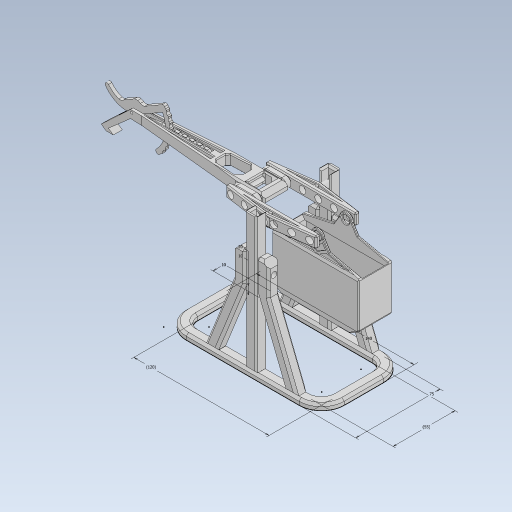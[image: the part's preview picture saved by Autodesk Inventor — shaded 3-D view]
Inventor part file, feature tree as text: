
AUTODESK INVENTOR PART (.ipt)
format: ipt  version: 2023 (Build 270158030, 158C)  size: 2,156,544 bytes
history: native  units: mm
features: extrude x40, chamfer x35, sketch x32, other x22, projected_geometry x18, fillet x12, mirror x11, plane x5, pattern_circular x2
ambient origin geometry x8: Origin, YZ Plane, XZ Plane, XY Plane, X Axis, Y Axis, Z Axis, Center Point
bodies: SOLID_WEIGHT (feature_tree)
feature tree (177):
  other  "baseplate"
  sketch  "Sketch1"  dims[d0=75.0mm d1=140.0mm]
  extrude  "Extrusion1"  Depth=140.0mm
  extrude  "Extrusion2"  Depth=10.0mm
  sketch  "Sketch3"  dims[d4=20.0mm d5=5.0mm d6=0.0mm]
  extrude  "Extrusion5"  Depth=5.0mm TaperAngle=0.0deg
  extrude  "Extrusion6"  Depth=2.0mm
  extrude  "Extrusion3"  Depth=3.0mm
  extrude  "Extrusion7"  Depth=10.0mm
  extrude  "Extrusion9"  TaperAngle=0.0deg  [1 undecoded]
  extrude  "Extrusion10"  Depth=120.0mm
  extrude  "Extrusion11"  Depth=0.01mm
  extrude  "Extrusion29"  Depth=10.0mm
  other  "center-mirror-plane"
  other  "Work Point1"
  plane  "Work Plane2"
  extrude  "Extrusion12"  Depth=25.0mm
  extrude  "Extrusion13"  Depth=5.0mm TaperAngle=0.0deg
  extrude  "Extrusion14"  Depth=10.0mm
  extrude  "Extrusion15"  Depth=10.0mm TaperAngle=0.0deg
  extrude  "Extrusion30"  Depth=5.0mm
  extrude  "Extrusion31"  Depth=6.5mm
  plane  "Work Plane5"
  extrude  "Extrusion32"  Depth=1.75mm
  extrude  "Extrusion33"  Depth=6.5mm
  extrude  "Extrusion34"  Depth=10.0mm
  fillet  "Fillet4"  Radius=3.2mm
  chamfer  "Chamfer37"  Distance=10.0mm
  extrude  "Extrusion35"  Depth=4.0mm
  chamfer  "Chamfer38"  [1 undecoded]
  fillet  "Fillet11"  Radius=21.0mm
  chamfer  "Chamfer39"  Distance=125.0mm
  fillet  "Fillet12"  Radius=10.0mm
  extrude  "Extrusion36"  Depth=1.5mm
  fillet  "Fillet5"  Radius=12.0mm
  extrude  "ratchet-extrusion"  TaperAngle=0.0deg  [1 undecoded]
  sketch  "Sketch51"  dims[d101=6.5mm]
  extrude  "Extrusion45"  Depth=1.5mm
  extrude  "Extrusion46"  Depth=1.5mm
  pattern_circular  "Circular Pattern3"  [2 undecoded]
  pattern_circular  "Circular Pattern4"  Angle=45.0deg  [1 undecoded]
  fillet  "Fillet13"  Radius=1.0mm
  fillet  "Fillet15"  Radius=1.5mm
  fillet  "Fillet10"  Radius=2.5mm
  extrude  "Extrusion17"  Depth=1.5mm
  extrude  "Extrusion26"  Depth=1.5mm
  extrude  "Extrusion38"  TaperAngle=0.0deg  [1 undecoded]
  extrude  "Extrusion47"  Depth=1.5mm
  fillet  "Fillet19"  Radius=2.0mm
  fillet  "Fillet16"  Radius=1.0mm
  chamfer  "Chamfer1"  Distance=1.5mm Angle=45.0deg
  chamfer  "Chamfer2"  Distance=1.5mm Angle=45.0deg
  chamfer  "Chamfer4"  Distance=2.0mm Angle=45.0deg
  chamfer  "Chamfer56"  Distance=1.5mm Angle=45.0deg
  extrude  "Extrusion19"  Depth=1.5mm
  chamfer  "Chamfer5"  Distance=8.0mm
  chamfer  "Chamfer8"  Distance=5.0mm
  chamfer  "Chamfer9"  Distance=28.0mm
  chamfer  "Chamfer10"  Distance=6.0mm
  extrude  "Extrusion39"  Depth=1.5mm
  mirror  "Mirror12"
  chamfer  "Chamfer11"  Distance=5.0mm
  chamfer  "Chamfer50"  Distance=28.0mm
  chamfer  "Chamfer12"  Distance=8.0mm
  plane  "Work Plane4"
  extrude  "CW-extrusion"  Depth=1.5mm
  mirror  "Mirror3"
  extrude  "Extrusion21"  Depth=1.5mm
  extrude  "Extrusion22"  Depth=1.5mm TaperAngle=0.0deg
  mirror  "Mirror4"
  chamfer  "Chamfer13"  Distance=2.0mm
  extrude  "Extrusion23"  Depth=1.5mm TaperAngle=0.0deg
  mirror  "Mirror5"
  chamfer  "Chamfer31"  Distance=1.5mm Angle=45.0deg
  chamfer  "Chamfer14"  Distance=1.5mm
  chamfer  "Chamfer17"  Distance=1.0mm Angle=45.0deg
  chamfer  "Chamfer18"  Distance=0.5mm Angle=45.0deg
  extrude  "Extrusion24"  Depth=0.5mm TaperAngle=45.0deg
  extrude  "Extrusion25"  TaperAngle=0.0deg  [1 undecoded]
  chamfer  "Chamfer20"  Distance=1.0mm
  chamfer  "Chamfer49"  Distance=1.0mm
  chamfer  "Chamfer21"  [1 undecoded]
  extrude  "Extrusion40"  Depth=4.0mm TaperAngle=45.0deg
  extrude  "Extrusion41"  Depth=1.5mm TaperAngle=45.0deg
  chamfer  "Chamfer22"  Distance=1.2mm Angle=45.0deg
  chamfer  "Chamfer44"  Distance=1.2mm
  chamfer  "Chamfer45"  Distance=3.0mm
  fillet  "Fillet3"  Radius=2.0mm
  mirror  "Mirror2"
  mirror  "Mirror1"
  plane  "Work Plane3"
  mirror  "Mirror6"
  mirror  "Mirror7"
  mirror  "Mirror8"
  chamfer  "Chamfer26"  Distance=2.0mm
  chamfer  "Chamfer27"  Distance=2.0mm
  extrude  "Extrusion43"  Depth=1.5mm
  mirror  "Mirror10"
  chamfer  "Chamfer47"  Distance=15.996982mm
  extrude  "Extrusion42"  Depth=1.5mm
  chamfer  "Chamfer48"  Distance=6.0mm
  mirror  "Mirror11"
  plane  "Work Plane6"
  chamfer  "Chamfer51"  Distance=6.0mm
  chamfer  "Chamfer52"  Distance=6.0mm
  fillet  "Fillet17"  Radius=5.0mm
  chamfer  "Chamfer53"  Distance=5.0mm
  chamfer  "Chamfer54"  Distance=14.0mm
  chamfer  "Chamfer55"  Distance=14.0mm
  fillet  "Fillet18"  [1 undecoded]
  chamfer  "Chamfer57"  Distance=3.5mm Angle=45.0deg
  sketch  "Sketch2"  dims[d2=10.0mm d3=10.0mm]
  sketch  "Sketch4"  dims[d7=6.0mm d9=2.0mm]
  projected_geometry  "Projected Loop1"
  other  "A-frame"
  sketch  "Sketch7"  dims[d10=10.0mm d11=3.0mm]
  projected_geometry  "Projected Loop2"
  other  "upright"
  sketch  "Sketch9"  dims[d12=1.75mm d13=6.0mm d14=10.0mm]
  projected_geometry  "Projected Loop3"
  sketch  "Sketch10"  dims[d15=60.0mm d16=0.0mm d17=0.0mm]
  sketch  "Sketch12"  dims[d18=55.0mm d19=120.0mm]
  sketch  "Sketch13"  dims[d22=0.1mm d23=0.01mm]
  sketch  "Sketch14"  dims[d24=5.0mm d25=0.0mm d38=10.0mm]
  other  "pivot"
  sketch  "Sketch16"  dims[d39=25.0mm d40=25.0mm]
  other  "throw-arm-top"
  sketch  "Sketch18"  dims[d41=0.1mm d42=5.0mm d43=5.0mm d44=0.0mm d45=0.0mm]
  sketch  "Sketch20"  dims[d47=10.0mm d50=10.0mm]
  sketch  "Sketch22"  dims[d51=120.0mm d52=0.0mm d53=10.0mm d54=0.0mm]
  other  "counterweight"
  projected_geometry  "Projected Loop5"
  sketch  "Sketch26"  dims[d60=5.0mm d61=5.0mm]
  projected_geometry  "Projected Loop6"
  sketch  "Sketch27"  dims[d64=0.0mm d65=0.0mm d66=6.5mm]
  projected_geometry  "Projected Loop7"
  sketch  "Sketch30"  dims[d67=1.75mm d68=1.75mm]
  other  "Pattern of pivot:1"
  other  "pivot-mirror"
  other  "Pattern of upright:2"
  other  "upright-mirror"
  other  "Pattern of A-frame:3"
  other  "A-frame-b"
  other  "Pattern of A-frame:4"
  other  "A-frame-c"
  other  "Pattern of A-frame-b:5"
  other  "A-frame-d"
  sketch  "Sketch31"  dims[d69=11.0mm d70=6.5mm]
  projected_geometry  "Projected Loop8"
  sketch  "Sketch32"  dims[d71=7.0mm d72=0.0mm d73=6.0mm d74=3.2mm d75=10.0mm d76=0.0mm]
  projected_geometry  "Projected Loop9"
  sketch  "Sketch34"  dims[d77=4.0mm d78=40.0mm]
  sketch  "Sketch36"  dims[d79=40.0mm]
  sketch  "Sketch37"  dims[d80=5.0mm]
  projected_geometry  "Projected Loop15"
  projected_geometry  "Projected Loop16"
  sketch  "Sketch39"  dims[d83=4.0mm]
  sketch  "Sketch40"  dims[d84=29.0mm]
  projected_geometry  "Projected Loop17"
  sketch  "Sketch43"  dims[d85=2.0mm d86=8.0mm d87=0.0mm d88=0.0mm]
  other  "ratchet"
  sketch  "Sketch44"  dims[d89=6.0mm]
  sketch  "Sketch45"  dims[d90=5.0mm]
  projected_geometry  "Projected Loop18"
  sketch  "Sketch46"  dims[d91=5.0mm d92=0.0mm d93=0.0mm d96=21.0mm]
  projected_geometry  "Projected Loop20"
  sketch  "Sketch48"  dims[d99=8.0mm]
  other  "spacer-a"
  other  "Pattern of spacer-a:6"
  other  "spacer-b"
  projected_geometry  "Projected Loop24"
  sketch  "Sketch49"  dims[d100=10.0mm]
  projected_geometry  "Projected Loop25"
  projected_geometry  "Projected Loop26"
  projected_geometry  "Projected Loop27"
  sketch  "Sketch52"  dims[d102=6.5mm d103=125.0mm d104=10.0mm d105=5.0mm d106=0.0mm d107=0.0mm d108=7.0mm d109=12.0mm d110=0.0mm d111=0.0mm d119=6.0mm d120=5.0mm d121=10.0mm d122=0.0mm d126=1.0mm d127=2.0mm d128=45.0deg d129=1.0mm d130=2.0mm d131=45.0deg d135=1.5mm d136=2.0mm d137=45.0deg d138=2.5mm d139=2.8mm d140=12.0mm d141=0.0mm d142=0.0mm d144=6.0mm d145=2.0mm d146=2.0mm d147=45.0deg d155=1.0mm d156=2.0mm d157=45.0deg d158=1.5mm d159=2.0mm d160=45.0deg d162=1.5mm d163=2.0mm d164=45.0deg d165=2.0mm d166=2.0mm d167=45.0deg d168=1.5mm d169=2.0mm d170=45.0deg d172=2.0mm d173=8.0mm d174=5.0mm d175=28.0mm d176=6.0mm d177=40.0mm d178=5.0mm d179=28.0mm d180=8.0mm d181=8.0mm d182=2.0mm d183=2.0mm d184=0.0mm d185=2.0mm d186=0.0mm d187=1.5mm d188=0.0mm d189=1.5mm d190=2.0mm d191=45.0deg d195=1.0mm d196=1.5mm d197=0.0mm d200=1.0mm d201=2.0mm d202=45.0deg d209=0.5mm d210=2.0mm d211=45.0deg d212=0.5mm d213=2.0mm d214=45.0deg d221=0.0mm d222=0.0mm d223=1.0mm d224=1.0mm d227=0.0mm d228=0.0mm d232=4.0mm d233=2.0mm d234=45.0deg d235=1.0mm d236=2.0mm d237=45.0deg d238=1.2mm d239=2.0mm d240=45.0deg d241=1.2mm d242=3.0mm d247=2.0mm d248=2.0mm d249=2.0mm d250=0.9mm d254=15.996982mm d255=8.0mm d256=6.0mm d257=6.0mm d258=6.0mm d259=5.0mm d260=5.0mm d261=14.0mm d262=14.0mm d263=0.0mm d264=0.0mm d271=3.5mm d272=2.0mm d273=45.0deg d274=3.5mm d275=2.0mm d276=45.0deg d287=1.5mm d288=2.0mm d289=45.0deg d290=1.9mm d291=10.0mm d292=0.0mm d298=3.0mm d299=0.5mm d300=0.0mm d303=3.5mm d304=3.0mm d305=0.5mm d306=0.0mm d307=2.1mm d310=0.0mm d311=0.0mm d312=5.2mm d313=10.0mm d314=0.8mm d315=27.1mm d316=3.2mm d317=0.0mm d319=0.0mm d320=0.0mm d321=36.0mm d322=0.4mm d323=0.4mm d324=3.5mm d328=3.2mm d329=0.0mm d331=4.0mm d337=3.2mm d338=0.0mm d343=3.2mm d344=3.2mm d345=3.2mm d346=3.2mm d347=3.2mm d348=3.2mm d349=3.2mm d350=3.2mm d351=1.9mm d352=0.0mm d353=4.0mm d363=19.6mm d364=19.5mm d366=3.0mm d367=90.0deg d368=23.0mm d377=10.0mm d386=2.9mm d387=0.0mm d394=1.7mm d396=4.4mm d398=3.5mm d399=2.0mm d400=45.0deg d401=3.0mm d402=2.0mm d403=45.0deg d404=4.0mm d405=2.5mm d406=2.0mm d407=45.0deg d408=4.0mm d415=4.0mm d426=1.5mm d431=7.0mm d432=0.0mm d433=0.0mm d434=4.0mm d438=1.0mm d439=2.4mm d440=0.0mm d441=0.8mm d447=14.0mm d448=14.0mm d449=14.0mm d450=10.0mm d451=0.0mm d454=4.0mm d455=0.0mm d456=2.0mm d457=2.0mm d458=45.0deg d459=0.7mm d460=2.0mm d461=45.0deg d465=12.0mm d466=12.0mm d467=5.0mm d468=25.0mm d469=5.0mm d470=3.0mm d471=0.8mm d472=2.0mm d473=45.0deg d474=1.5mm d475=0.15mm d476=5.0mm d477=0.0mm d478=0.6mm d479=2.0mm d480=45.0deg d481=5.0mm d483=38.5mm d484=38.5mm d485=2.5mm d491=2.0mm d492=30.0deg d493=14.0mm d494=0.5mm d495=2.0mm d496=45.0deg d497=2.5mm d498=2.5mm d499=30.0deg d500=1.5mm d501=0.0mm d505=11.0mm d506=5.0mm d507=2.0mm d508=45.0deg d510=75.0deg d512=0.4mm d514=10.293981mm d520=1.5mm d521=63.0mm d522=3.2mm d524=4.0mm d525=75.0deg d526=35.0mm d527=5.072433mm d528=2.3mm d529=4.5mm d530=1.2mm d531=2.9mm d532=0.0mm d533=1.5mm d534=0.0mm d535=0.0mm d542=40.0mm d543=4.363323mm d545=50.0mm d546=5.759587mm d548=5.5mm d549=38.0mm d550=10.902886mm d551=5.0mm d552=2.0mm d553=45.0deg d554=1.0mm d555=2.0mm d556=45.0deg d557=2.0mm d558=2.0mm d559=0.0mm d560=1.0mm d561=2.0mm d562=45.0deg d563=1.9mm d564=2.0mm d565=45.0deg d566=1.6mm d567=2.0mm d568=45.0deg d570=7.0mm d572=7.504916mm d574=27.229453mm d575=2.0mm d576=0.95mm d577=0.7mm d578=4.362765mm d579=28.01763mm d580=40.653421mm d581=6.0mm d582=3.2mm d583=30.0deg d584=3.0mm d591=0.9mm d592=0.9mm d593=39.249188mm d594=1.5mm d595=1.5mm d596=3.0mm d597=3.0mm d598=5.0mm d599=2.501152mm d600=2.562412mm d601=3.0mm d602=90.0mm d603=10.765796mm d604=0.5mm d605=2.0mm d606=45.0deg d607=1.5mm d608=1.5mm d609=1.0mm d610=2.0mm d611=45.0deg d612=4.5mm d613=0.0mm d614=0.0mm d615=1.5mm]
  projected_geometry  "Projected Loop28"
note: 10 required parameter values undecoded (feature->parameter linkage not recoverable at this tier; creation-order binding heuristic only, values carry confidence <= 0.55)
